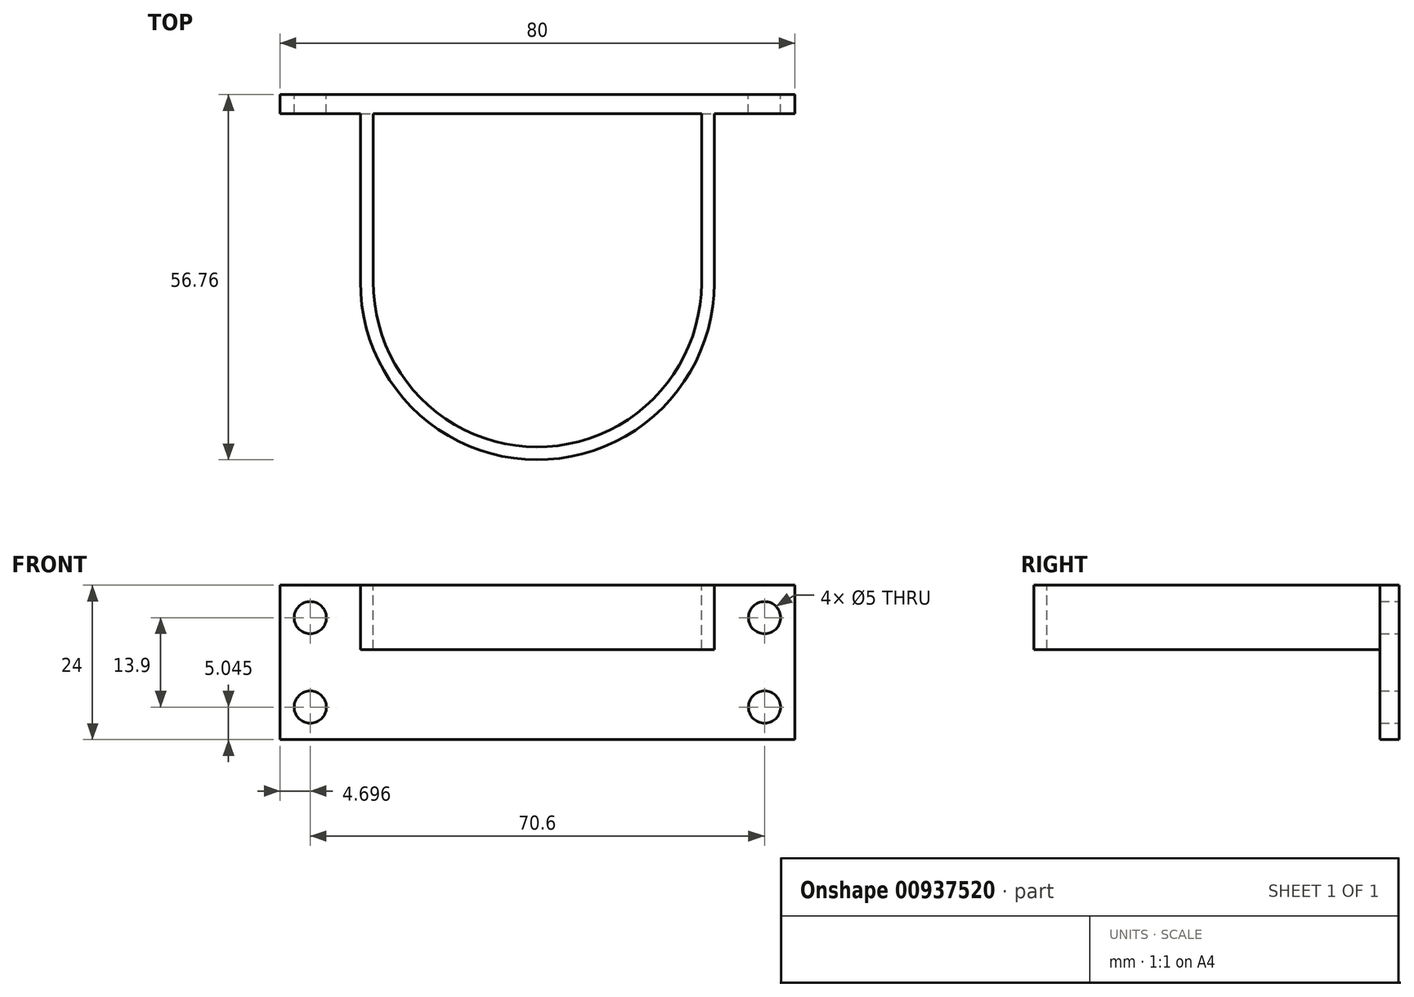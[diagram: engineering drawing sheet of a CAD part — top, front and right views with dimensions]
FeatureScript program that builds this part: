
annotation { "Feature Type Name" : "Feature", "Feature Type Description" : "" }
export const myFeature = defineFeature(function(context is Context, id is Id, definition is map)
    precondition{}
    {
        {
            var Q0;
            Q0=qCreatedBy(makeId("Front.planeOp"),FACE);
            var sketch = newSketch(context, id + "F0", { "sketchPlane" : qUnion([Q0])});
            skLineSegment(sketch, "E0.bottom", {"start": v(-46.64, 13.32) * mm, "end": v(33.36, 13.32) * mm});
            skLineSegment(sketch, "E0.top", {"start": v(-46.64, -10.68) * mm, "end": v(33.36, -10.68) * mm});
            skLineSegment(sketch, "E0.left", {"start": v(-46.64, 13.32) * mm, "end": v(-46.64, -10.68) * mm});
            skLineSegment(sketch, "E0.right", {"start": v(33.36, 13.32) * mm, "end": v(33.36, -10.68) * mm});
            skCircle(sketch, "E1", {"center": v(-41.94, 8.27) * mm, "radius": 2.5 * mm});
            skLineSegment(sketch, "E2", {"start": v(-6.64, 13.32) * mm, "end": v(-6.64, -10.68) * mm, "construction": true});
            skLineSegment(sketch, "E3", {"start": v(-46.64, 1.32) * mm, "end": v(33.36, 1.32) * mm, "construction": true});
            skCircle(sketch, "E4.MirrorC", {"center": v(28.66, 8.27) * mm, "radius": 2.5 * mm});
            skCircle(sketch, "E5.MirrorC", {"center": v(-41.94, -5.63) * mm, "radius": 2.5 * mm});
            skCircle(sketch, "E6.MirrorC", {"center": v(28.66, -5.63) * mm, "radius": 2.5 * mm});
            skSolve(sketch);
        }
        {
            var Q0;
            Q0=makeQuery(id+"F0.imprint","IMPRINT",FACE,{"disambiguationData":[TD([[makeQuery(id+"F0.imprint","IMPRINT",EDGE,{"derivedFrom":sQuery(id+"F0.wireOp",EDGE,"E0.bottom")}),-1.0]])]});
            extrude(context, id + "F1", {"entities" : qUnion([Q0]), "depth" : 3 * mm, "offsetDistance" : 25 * mm});
        }
        {
            var Q0;
            Q0=makeQuery(id+"F1.opExtrude","SWEPT_FACE",FACE,{"disambiguationData":[OSD([sQuery(id+"F0.wireOp",EDGE,"E0.bottom")])]});
            var sketch = newSketch(context, id + "F2", { "sketchPlane" : qUnion([Q0])});
            skArc(sketch, "E7", {"start": v(-32.14, -29.1) * mm, "mid": v(-6.76, -54.76) * mm, "end": v(18.86, -29.32) * mm});
            skPoint(sketch, "E7.centerSnap0", {"position": v(-6.64, -3) * mm});
            skLineSegment(sketch, "E8", {"start": v(-32.14, -29.1) * mm, "end": v(-32.14, -3) * mm});
            skLineSegment(sketch, "E9", {"start": v(18.86, -29.32) * mm, "end": v(18.86, -3) * mm});
            skLineSegment(sketch, "E10.0", {"start": v(-34.14, -29.09) * mm, "end": v(-34.14, -3) * mm});
            skArc(sketch, "E10.1", {"start": v(-34.14, -29.09) * mm, "mid": v(-6.76, -56.76) * mm, "end": v(20.86, -29.32) * mm});
            skLineSegment(sketch, "E10.2", {"start": v(20.86, -29.32) * mm, "end": v(20.86, -3) * mm});
            skSolve(sketch);
        }
        {
            var Q0;
            Q0=makeQuery(id+"F2.imprint","IMPRINT",FACE,{"disambiguationData":[TD([[makeQuery(id+"F2.imprint","IMPRINT",EDGE,{"derivedFrom":sQuery(id+"F2.wireOp",EDGE,"E7")}),-1.0]])]});
            extrude(context, id + "F3", {"entities" : qUnion([Q0]), "operationType" : NewBodyOperationType.ADD, "oppositeDirection" : true, "depth" : 10 * mm, "offsetDistance" : 25 * mm});
        }
    });
